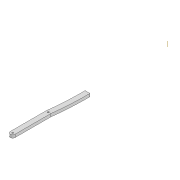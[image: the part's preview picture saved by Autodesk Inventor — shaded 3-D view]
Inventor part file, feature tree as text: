
AUTODESK INVENTOR PART (.ipt)
format: ipt  version: 2022 (Build 260153000, 153)  size: 109,056 bytes
history: native  units: mm
features: extrude x2, sketch x2, other x1
ambient origin geometry x8: Origin, YZ Plane, XZ Plane, XY Plane, X Axis, Y Axis, Z Axis, Center Point
bodies: Solid1 (feature_tree)
feature tree (5):
  extrude  "Extrusion1"  Depth=3.3mm
  other  "Work Axis3"
  extrude  "Extrusion2"  Depth=600.0mm
  sketch  "Sketch1"  dims[d0=3.3mm d1=3.3mm]
  sketch  "Sketch2"  dims[d2=10.0mm d3=322.934mm d4=3.3mm d5=74.182mm d6=6.0mm d7=0.0mm d8=3.3mm d9=218.733mm d12=600.0mm d13=600.0mm d14=100.0mm d15=0.0mm]
